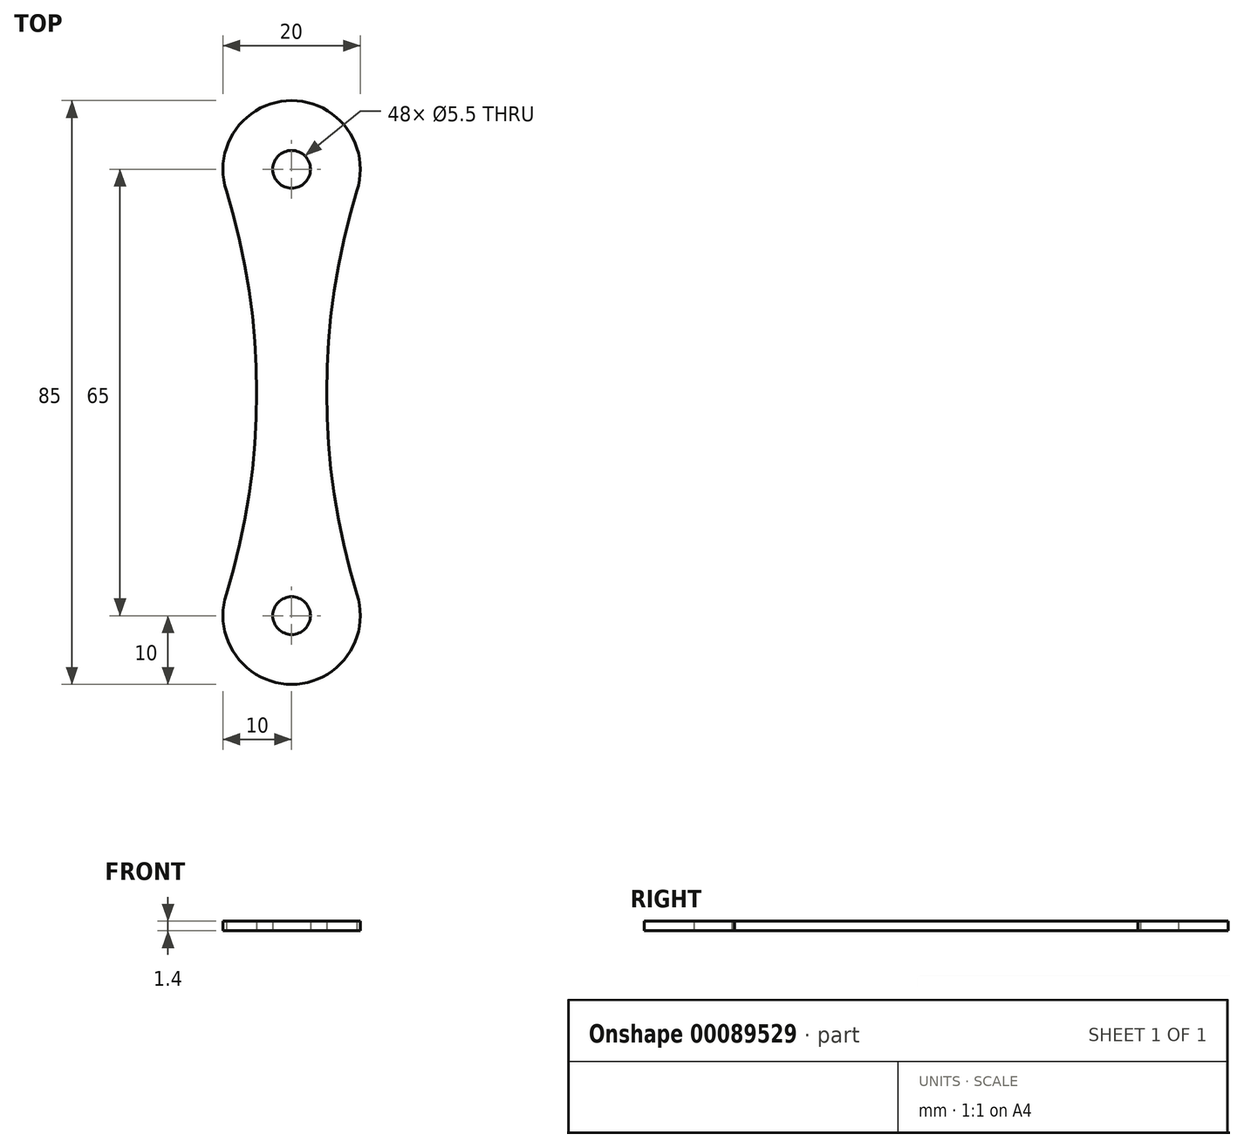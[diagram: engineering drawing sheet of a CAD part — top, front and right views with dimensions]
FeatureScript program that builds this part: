
annotation { "Feature Type Name" : "Feature", "Feature Type Description" : "" }
export const myFeature = defineFeature(function(context is Context, id is Id, definition is map)
    precondition{}
    {
        {
            var Q0;
            Q0=qCreatedBy(makeId("Top.planeOp"),FACE);
            var sketch = newSketch(context, id + "F0", { "sketchPlane" : qUnion([Q0])});
            skCircle(sketch, "E0", {"center": v(0, 35.25) * mm, "radius": 2.75 * mm});
            skCircle(sketch, "E1", {"center": v(0, -29.75) * mm, "radius": 2.75 * mm});
            skArc(sketch, "E2", {"start": v(9.5, 32.13) * mm, "mid": v(0, 45.25) * mm, "end": v(-9.5, 32.13) * mm});
            skArc(sketch, "E3", {"start": v(-9.5, -26.63) * mm, "mid": v(0, -39.75) * mm, "end": v(9.5, -26.63) * mm});
            skArc(sketch, "E4", {"start": v(-9.5, -26.63) * mm, "mid": v(-5.09, 2.75) * mm, "end": v(-9.5, 32.13) * mm});
            skArc(sketch, "E5.MirrorCS", {"start": v(9.5, -26.63) * mm, "mid": v(5.09, 2.75) * mm, "end": v(9.5, 32.13) * mm});
            skSolve(sketch);
        }
        {
            var Q0;
            Q0 = qSketchRegion(id + "F0", true);
            extrude(context, id + "F1", {"entities" : qUnion([Q0]), "depth" : 1.4 * mm});
        }
    });
